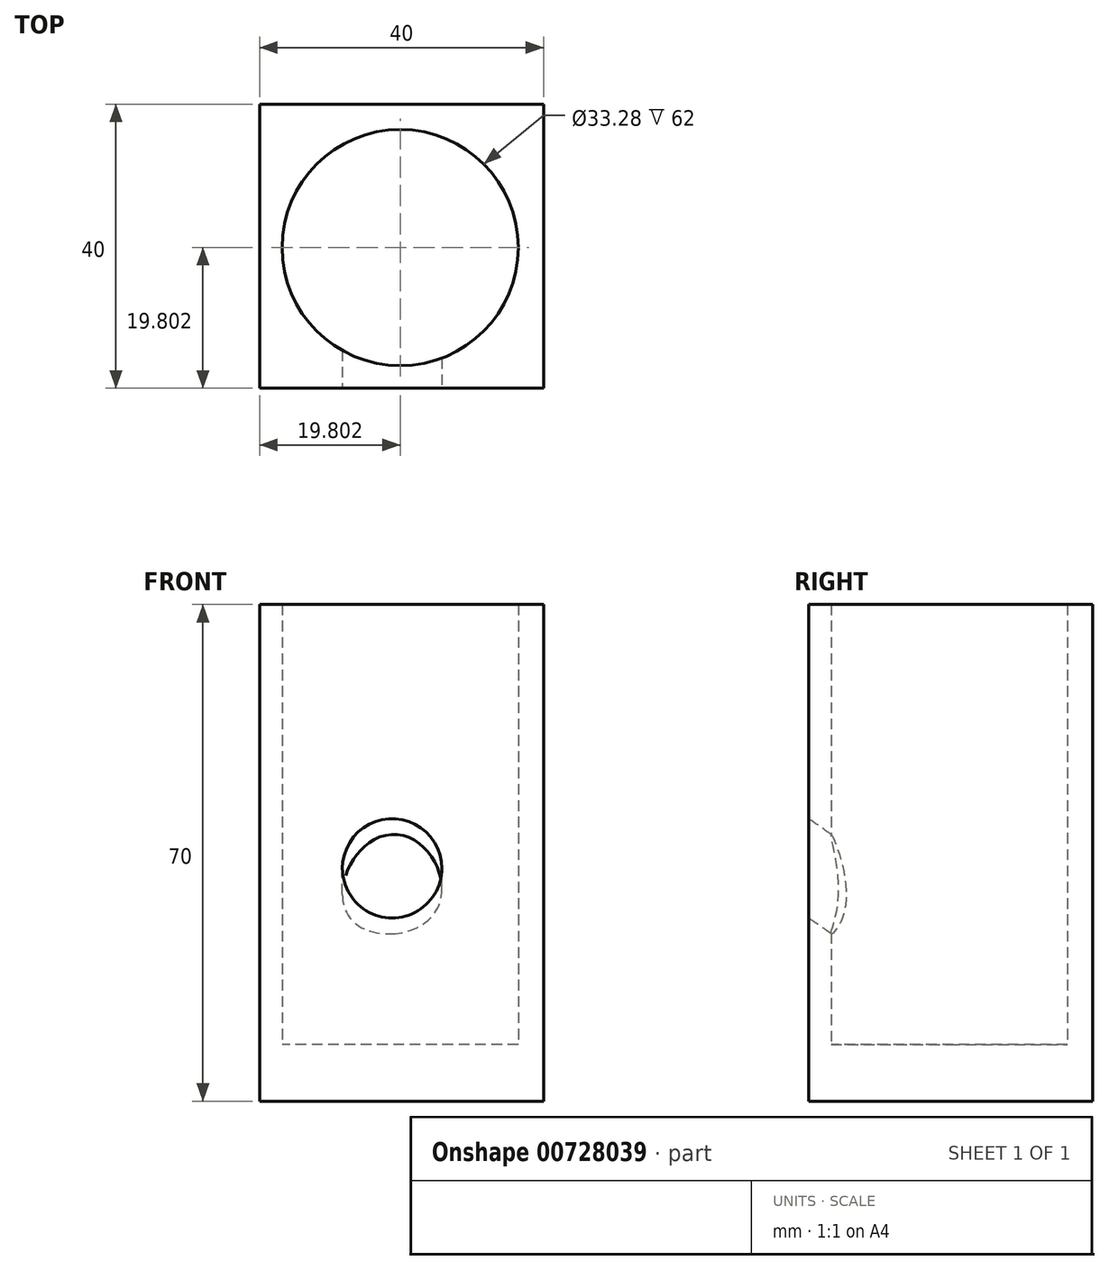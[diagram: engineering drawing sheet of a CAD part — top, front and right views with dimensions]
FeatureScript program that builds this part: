
annotation { "Feature Type Name" : "Feature", "Feature Type Description" : "" }
export const myFeature = defineFeature(function(context is Context, id is Id, definition is map)
    precondition{}
    {
        {
            var Q0;
            Q0=qCreatedBy(makeId("Top.planeOp"),FACE);
            var sketch = newSketch(context, id + "F0", { "sketchPlane" : qUnion([Q0])});
            skLineSegment(sketch, "E0.bottom", {"start": v(0, 0) * mm, "end": v(40, 0) * mm});
            skLineSegment(sketch, "E0.top", {"start": v(0, 40) * mm, "end": v(40, 40) * mm});
            skLineSegment(sketch, "E0.left", {"start": v(0, 0) * mm, "end": v(0, 40) * mm});
            skLineSegment(sketch, "E0.right", {"start": v(40, 0) * mm, "end": v(40, 40) * mm});
            skSolve(sketch);
        }
        {
            var Q0;
            Q0 = qSketchRegion(id + "F0", true);
            extrude(context, id + "F1", {"entities" : qUnion([Q0]), "depth" : 70 * mm, "offsetDistance" : 25 * mm});
        }
        {
            var Q0;
            Q0=qCreatedBy(makeId("Top.planeOp"),FACE);
            var sketch = newSketch(context, id + "F2", { "sketchPlane" : qUnion([Q0])});
            skCircle(sketch, "E1", {"center": v(19.8, 19.8) * mm, "radius": 16.64 * mm});
            skSolve(sketch);
        }
        {
            var Q0;
            Q0 = qSketchRegion(id + "F2", true);
            extrude(context, id + "F3", {"entities" : qUnion([Q0]), "operationType" : NewBodyOperationType.REMOVE, "depth" : 80 * mm, "offsetDistance" : 25 * mm});
        }
        {
            var Q0;
            Q0=qCreatedBy(makeId("Top.planeOp"),FACE);
            var sketch = newSketch(context, id + "F4", { "sketchPlane" : qUnion([Q0])});
            skLineSegment(sketch, "E2.bottom", {"start": v(0, 0) * mm, "end": v(40, 0) * mm});
            skLineSegment(sketch, "E2.top", {"start": v(0, 40) * mm, "end": v(40, 40) * mm});
            skLineSegment(sketch, "E2.left", {"start": v(0, 0) * mm, "end": v(0, 40) * mm});
            skLineSegment(sketch, "E2.right", {"start": v(40, 0) * mm, "end": v(40, 40) * mm});
            skSolve(sketch);
        }
        {
            var Q0;
            Q0 = qSketchRegion(id + "F4", true);
            extrude(context, id + "F5", {"entities" : qUnion([Q0]), "operationType" : NewBodyOperationType.ADD, "depth" : 8 * mm, "offsetDistance" : 25 * mm});
        }
        {
            var Q0;
            Q0=qCreatedBy(makeId("Front.planeOp"),FACE);
            var sketch = newSketch(context, id + "F6", { "sketchPlane" : qUnion([Q0])});
            skCircle(sketch, "E3", {"center": v(18.65, 32.81) * mm, "radius": 7 * mm});
            skSolve(sketch);
        }
        {
            var Q0;
            Q0=qCreatedBy(makeId("Right.planeOp"),FACE);
            var sketch = newSketch(context, id + "F7", { "sketchPlane" : qUnion([Q0])});
            skLineSegment(sketch, "E4", {"start": v(-5.84, 26.9) * mm, "end": v(5.38, 19.12) * mm});
            skSolve(sketch);
        }
        {
            var Q0;
            Q0 = qSketchRegion(id + "F6", true);
            var Q1;
            Q1 = qConstructionFilter(qBodyType(qCreatedBy(id + "F7" ,EDGE), BodyType.WIRE), ConstructionObject.NO);
            sweep(context, id + "F8", {"operationType" : NewBodyOperationType.REMOVE, "profiles" : qUnion([Q0]), "path" : qUnion([Q1])});
        }
    });
